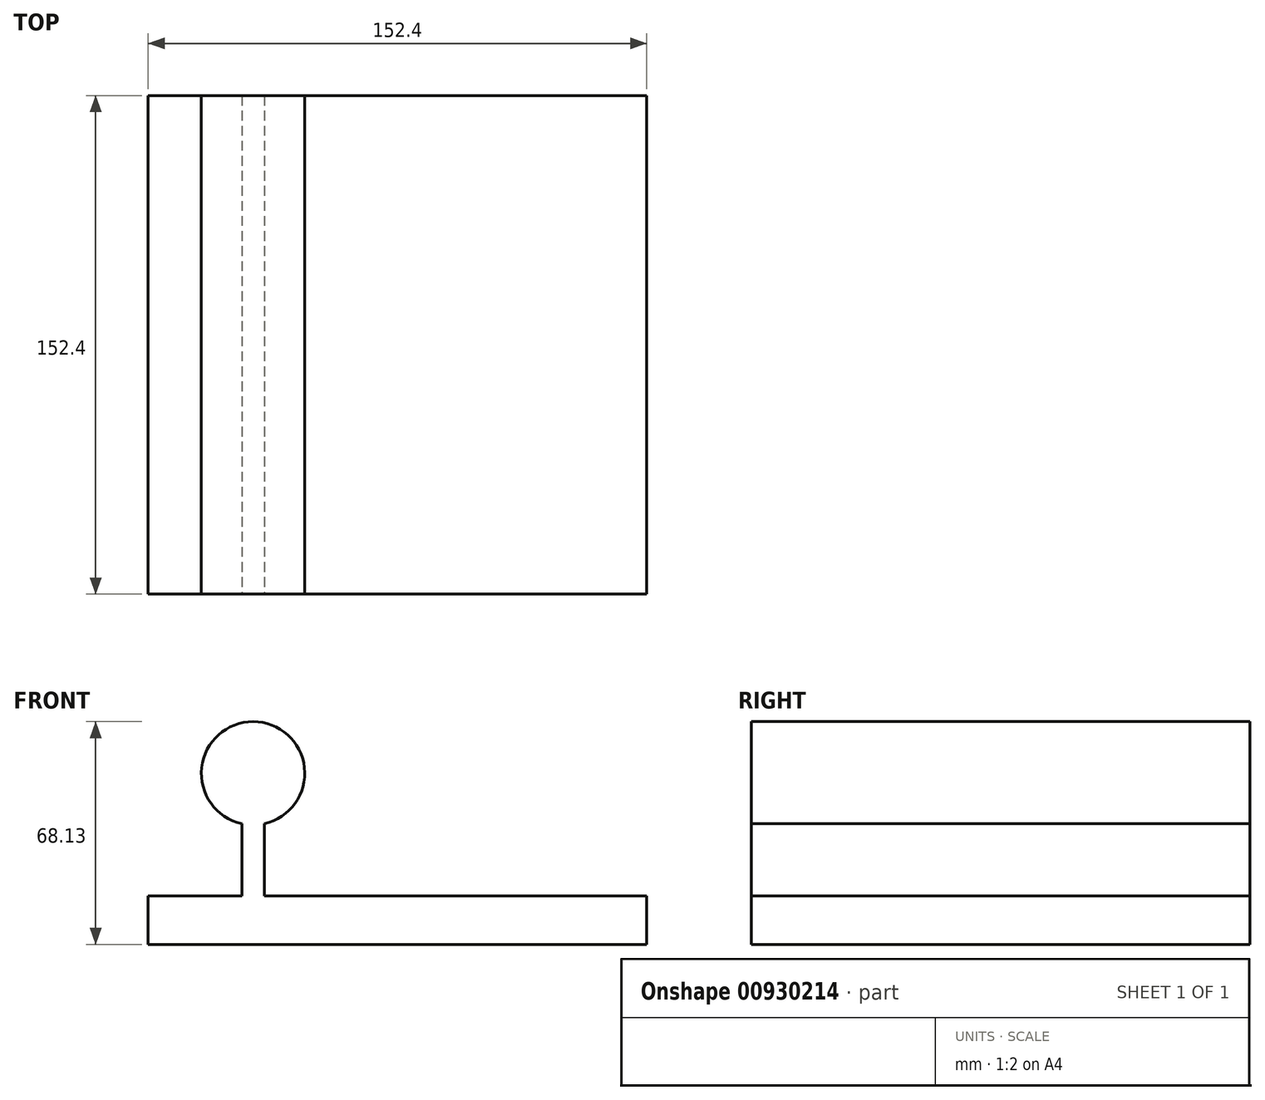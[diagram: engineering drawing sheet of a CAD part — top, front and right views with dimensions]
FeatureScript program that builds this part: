
annotation { "Feature Type Name" : "Feature", "Feature Type Description" : "" }
export const myFeature = defineFeature(function(context is Context, id is Id, definition is map)
    precondition{}
    {
        {
            var Q0;
            Q0=qCreatedBy(makeId("Front.planeOp"),FACE);
            var sketch = newSketch(context, id + "F0", { "sketchPlane" : qUnion([Q0])});
            skLineSegment(sketch, "E0", {"start": v(76.2, 0) * mm, "end": v(-76.2, 0) * mm});
            skLineSegment(sketch, "E1", {"start": v(-76.2, 0) * mm, "end": v(-76.2, 14.78) * mm});
            skLineSegment(sketch, "E2", {"start": v(-76.2, 14.78) * mm, "end": v(-47.58, 14.78) * mm});
            skLineSegment(sketch, "E3", {"start": v(-47.58, 14.78) * mm, "end": v(-47.58, 36.9) * mm});
            skLineSegment(sketch, "E4", {"start": v(76.2, 0) * mm, "end": v(76.2, 14.78) * mm});
            skLineSegment(sketch, "E5", {"start": v(76.2, 14.78) * mm, "end": v(-40.68, 14.78) * mm});
            skLineSegment(sketch, "E6", {"start": v(-40.68, 14.78) * mm, "end": v(-40.68, 36.9) * mm});
            skLineSegment(sketch, "E7", {"start": v(-40.68, 36.9) * mm, "end": v(-47.58, 36.9) * mm});
            skCircle(sketch, "E8", {"center": v(-44.13, 52.33) * mm, "radius": 15.8 * mm});
            skPoint(sketch, "E8.centerSnap0", {"position": v(-44.13, 36.9) * mm});
            skSolve(sketch);
        }
        {
            var Q0;
            Q0 = qSketchRegion(id + "F0", true);
            extrude(context, id + "F1", {"entities" : qUnion([Q0]), "oppositeDirection" : true, "depth" : 152.4 * mm, "offsetDistance" : 25.4 * mm});
        }
    });
